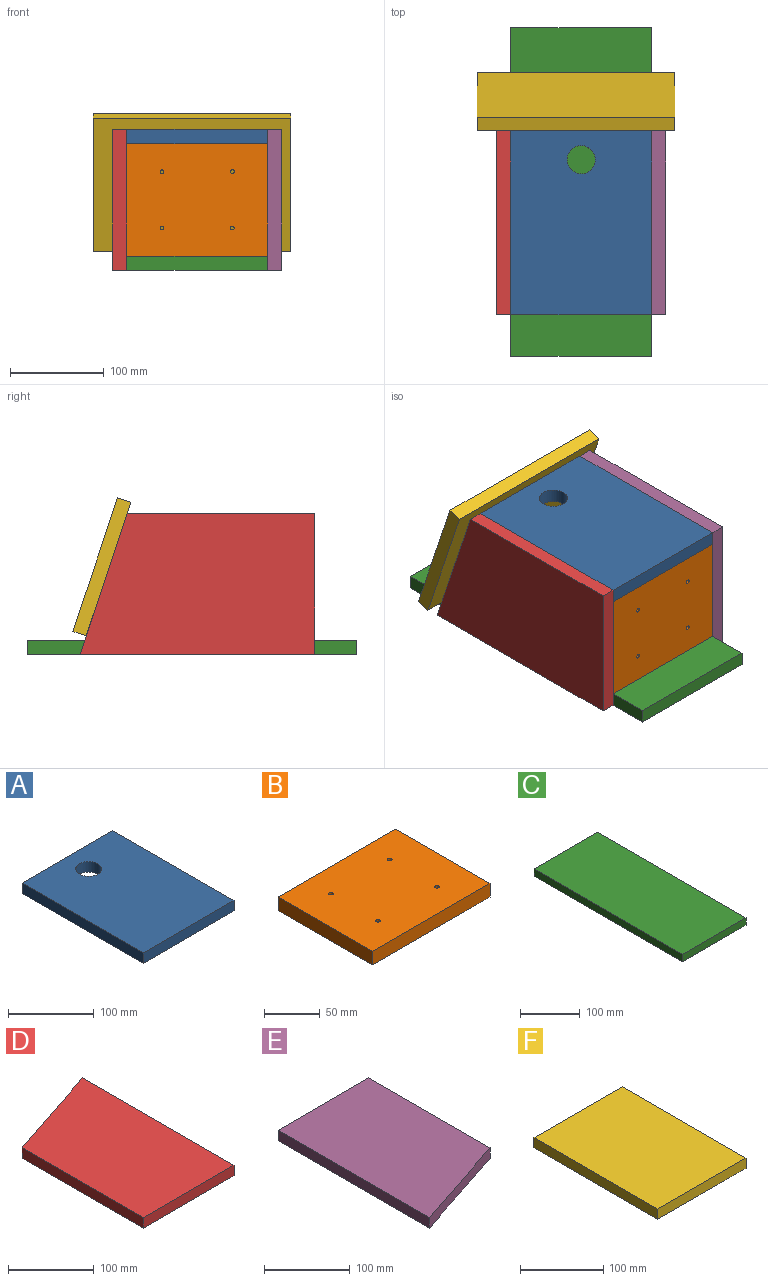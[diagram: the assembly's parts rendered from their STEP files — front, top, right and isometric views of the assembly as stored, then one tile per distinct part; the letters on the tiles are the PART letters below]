
ASSEMBLY  parts=6 mates=6
PART A: 7 faces, bbox 150x200x15 mm
  f0: plane 150x15mm, normal (0,1,0), area 2250mm2, adj f1,f3,f5,f6
  f1: plane 200x15mm, normal (-1,0,0), area 3000mm2, adj f0,f2,f5,f6
  f2: plane 150x15mm, normal (0,-1,0), area 2250mm2, adj f1,f3,f5,f6
  f3: plane 200x15mm, normal (1,0,0), area 3000mm2, adj f0,f2,f5,f6
  f4: cylinder r=15mm len=30mm, axis (0,0,-1), area 1413.7mm2, adj f5,f6
  f5: plane 200x150mm, normal (0,0,1), area 29293.1mm2, adj f0,f1,f2,f3,f4
  f6: plane 200x150mm, normal (0,0,-1), area 29293.1mm2, adj f0,f1,f2,f3,f4
PART B: 10 faces, bbox 150x120x15 mm
  f0: plane 150x15mm, normal (0,1,0), area 2250mm2, adj f1,f6,f8,f9
  f1: plane 120x15mm, normal (-1,0,0), area 1800mm2, adj f0,f2,f8,f9
  f2: plane 150x15mm, normal (0,-1,0), area 2250mm2, adj f1,f6,f8,f9
  f3: cylinder r=2mm len=15mm, axis (0,0,-1), area 188.5mm2, adj f8,f9
  f4: cylinder r=2mm len=15mm, axis (0,0,-1), area 188.5mm2, adj f8,f9
  f5: cylinder r=2mm len=15mm, axis (0,0,-1), area 188.5mm2, adj f8,f9
  f6: plane 120x15mm, normal (1,0,0), area 1800mm2, adj f0,f2,f8,f9
  f7: cylinder r=2mm len=15mm, axis (0,0,-1), area 188.5mm2, adj f8,f9
  f8: plane 150x120mm, normal (0,0,1), area 17949.7mm2, adj f0,f1,f2,f3,f4,f5,f6,f7
  f9: plane 150x120mm, normal (0,0,-1), area 17949.7mm2, adj f0,f1,f2,f3,f4,f5,f6,f7
PART C: 6 faces, bbox 150x350x15 mm
  f0: plane 350x150mm, normal (0,0,1), area 52500mm2, adj f1,f3,f4,f5
  f1: plane 350x15mm, normal (-1,0,0), area 5250mm2, adj f0,f2,f3,f4
  f2: plane 350x150mm, normal (0,0,-1), area 52500mm2, adj f1,f3,f4,f5
  f3: plane 150x15mm, normal (0,-1,0), area 2250mm2, adj f0,f1,f2,f5
  f4: plane 150x15mm, normal (0,1,0), area 2250mm2, adj f0,f1,f2,f5
  f5: plane 350x15mm, normal (1,0,0), area 5250mm2, adj f0,f2,f3,f4
PART D: 6 faces, bbox 150x250x15 mm
  f0: plane 250x150mm, normal (0,0,1), area 33750mm2, adj f1,f3,f4,f5
  f1: plane 200x15mm, normal (-1,0,0), area 3000mm2, adj f0,f2,f3,f4
  f2: plane 250x150mm, normal (0,0,-1), area 33750mm2, adj f1,f3,f4,f5
  f3: plane 150x15mm, normal (0,-1,0), area 2250mm2, adj f0,f1,f2,f5
  f4: plane 150x50mm, normal (-0.32,0.95,0), area 2371.7mm2, adj f0,f1,f2,f5
  f5: plane 250x15mm, normal (1,0,0), area 3750mm2, adj f0,f2,f3,f4
PART E: 6 faces, bbox 150x250x15 mm
  f0: plane 150x15mm, normal (0,1,0), area 2250mm2, adj f1,f3,f4,f5
  f1: plane 250x15mm, normal (-1,0,0), area 3750mm2, adj f0,f2,f4,f5
  f2: plane 150x50mm, normal (0.32,-0.95,0), area 2371.7mm2, adj f1,f3,f4,f5
  f3: plane 200x15mm, normal (1,0,0), area 3000mm2, adj f0,f2,f4,f5
  f4: plane 250x150mm, normal (0,0,1), area 33750mm2, adj f0,f1,f2,f3
  f5: plane 250x150mm, normal (0,0,-1), area 33750mm2, adj f0,f1,f2,f3
PART F: 6 faces, bbox 150x210x15 mm
  f0: plane 210x150mm, normal (0,0,1), area 31500mm2, adj f1,f3,f4,f5
  f1: plane 210x15mm, normal (-1,0,0), area 3150mm2, adj f0,f2,f3,f4
  f2: plane 210x150mm, normal (0,0,-1), area 31500mm2, adj f1,f3,f4,f5
  f3: plane 150x15mm, normal (0,-1,0), area 2250mm2, adj f0,f1,f2,f5
  f4: plane 150x15mm, normal (0,1,0), area 2250mm2, adj f0,f1,f2,f5
  f5: plane 210x15mm, normal (1,0,0), area 3150mm2, adj f0,f2,f3,f4
PLACE A at identity fixed
PLACE B rot(axis=(0,-0.71,0.71),180deg) t=(0,-635,-980)mm
PLACE C t=(0,635.87,-135)mm
PLACE D rot(axis=(0,1,0),90deg) t=(-90,-200,-60)mm
PLACE E rot(axis=(-0.71,0,-0.71),180deg) t=(75,-650,-60)mm
PLACE F rot(axis=(0.63,0.63,-0.45),131.2deg) t=(749.53,-416.05,-39.42)mm
MATE fastened E.f5 <-> A.f3  axis (-1,0,0) through (75,-650,15)mm
MATE planar F.f0 <-> D.f4  axis (0,-0.95,-0.32) through (99.53,-406.56,-115.31)mm
MATE planar C.f5 <-> E.f5  axis (1,0,0) through (75,-519.13,-127.5)mm
MATE fastened D.f0 <-> A.f1  axis (1,0,0) through (-75,-650,15)mm
MATE planar C.f2 <-> E.f1  axis (0,0,-1) through (0,-519.13,-135)mm
MATE fastened B.f2 <-> A.f6  axis (0,0,1) through (75,-650,0)mm
